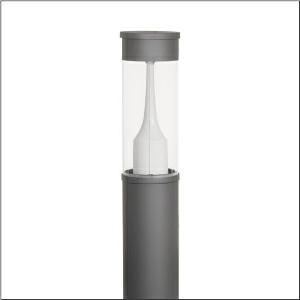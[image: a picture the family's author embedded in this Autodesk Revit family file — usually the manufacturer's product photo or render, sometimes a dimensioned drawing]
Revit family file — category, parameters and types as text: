
# Revit family: city-light_400_iq___p1_0a_5xa5305ff14h_0bc5
name_source: partatom
category: Lighting Fixtures
units: mm (PartAtom-declared; Revit-internal decimal feet)

## family parameters
Cut with Voids When Loaded = No
Host = Face
Light Source = No
Part Type = Normal
Room Calculation Point = No
Round Connector Dimension = Use Diameter
Shared = No

## types (1)
- --- (1 x LED, 1510 lm, 10.5 W, 3000K)
    Apparent Load = 11 VA
    CIE Flux Codes = 32 61 90 93 100
    Color Rendering = 70
    Color Temperature = 3000K
    Default Elevation = 1800 mm
    Description = City-Light 400 iQ, light pillar, Module 540 iQ-SR, primary light control with 3 zone facetted reflector, of plastic, silver coated, highly specular, structured, primary optical cover: cover, of PMMA, transparent, light distribution: P1.0a, primary light characteristic: strongly asymmetric, LED, High Power LED, rated luminous flux: 1.510lm, luminous efficacy: 144lm/W, light colour: 730, colour temperature: 3000K, control gear: ECG iQ, control: Auto-Match, Temp-Guard, Lumen-Switch, Night-Set, Smart-Wire, Light-Fading, Desk-Remote (wireless, voltage-free reading and setting of iQ features in the workshop via application-optimized NFC function/RFID function), optimised constant luminous flux control (CLO 2.0), Street-Remote, pre-setting: logarithmic dimming characteristic, with terminal, 6-pole, max. 2.5mm², mains connection: 230..240V, AC, 50/60Hz, start of lifetime: 11W, end of service life: 11W, reduction: 5W, luminaire housing, cylindrical, of extruded aluminium section, coated, Siteco® metallic grey (DB 702S), length: 4.694mm, diameter: 200mm, Module 540 iQ-SR, traffic white (RAL 9016), equipment: standard, protection rating (complete): IP65, insulation class (complete): insulation class II (safety insulation), certification: CE, ENEC, VDE, packaging unit: 1 piece

Light Distribution: P1.0a
    Height = 500 mm
    Lamp = 1 x LED
    Lamp Light Flux = 1510 lm
    Lamp Power = 10.5 W
    Lamp count = 1
    Length = 200 mm  [stored 0.656168 ft]
    Luminous efficacy = 144 lm/W
    Manufacturer = Siteco
    ModVariant = No
    Model = 5XA5305FF14H
    Mounting Place = Floor
    Mounting Type = Freestanding
    Number of Poles = 1
    OnlyDefault = Yes
    Power Factor = 1
    Product Name = City-Light 400 iQ | P1.0a
    Product group = light pillar
    ProductGroupID = 1301
    Protection Class = Protection class II
    Protection Degree = IP 65
    RLX_Detail_Level = 1
    RLX_Emergency_Light_Flux = 0 lm
    RLX_Emergency_Type = 0
    RLX_Emergency_Type_DB = No
    RlxData = <blob elided: 75377 chars, md5=c4d3779f>
    Socket = socket
    Standby Power = 0 W
    System Light Flux = 1510 lm
    System Power = 11 W
    Type Comments = factory setting: luminous flux: 100 % | dim-lin: 254 | 419 mA
    Type Image = l_1006914.jpg
    URL = http://relux.com
    VarID = @adj_129757
    Voltage = 0 V
    Weight = 0.00 kg
    Width = 0 mm  [stored 0 ft]

note: [stored X ft] marks values corroborated as IEEE doubles in the binary element streams (Revit-internal decimal feet)

## geometry (parser evidence)
native form markers: Blend x4, Sweep x9
no freeform markers — native parametric forms only
